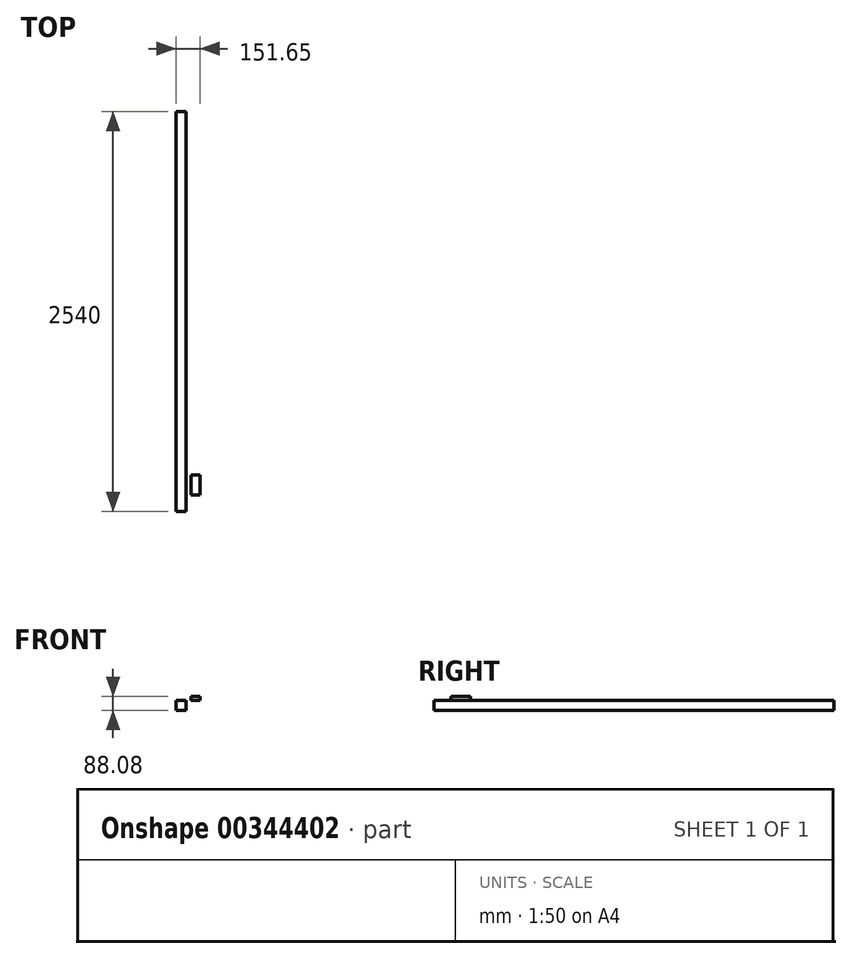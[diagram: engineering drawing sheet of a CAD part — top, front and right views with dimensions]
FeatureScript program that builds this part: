
annotation { "Feature Type Name" : "Feature", "Feature Type Description" : "" }
export const myFeature = defineFeature(function(context is Context, id is Id, definition is map)
    precondition{}
    {
        {
            var Q0;
            Q0=qCreatedBy(makeId("Front.planeOp"),FACE);
            var sketch = newSketch(context, id + "F0", { "sketchPlane" : qUnion([Q0])});
            skLineSegment(sketch, "E0", {"start": v(0, 0) * mm, "end": v(0, 0) * mm});
            skLineSegment(sketch, "E1.bottom", {"start": v(0, 0) * mm, "end": v(62.71, 0) * mm});
            skLineSegment(sketch, "E1.top", {"start": v(0, 62.68) * mm, "end": v(62.71, 62.68) * mm});
            skLineSegment(sketch, "E1.left", {"start": v(0, 0) * mm, "end": v(0, 62.68) * mm});
            skLineSegment(sketch, "E1.right", {"start": v(62.71, 0) * mm, "end": v(62.71, 62.68) * mm});
            skSolve(sketch);
        }
        {
            var Q0;
            Q0 = qSketchRegion(id + "F0", true);
            extrude(context, id + "F1", {"entities" : qUnion([Q0]), "depth" : 2540 * mm});
        }
        {
            var Q0;
            Q0=makeQuery(id+"F1.opExtrude","SWEPT_FACE",FACE,{"disambiguationData":[OSD([sQuery(id+"F0.wireOp",EDGE,"E1.top")])]});
            var sketch = newSketch(context, id + "F2", { "sketchPlane" : qUnion([Q0])});
            skLineSegment(sketch, "E2.bottom", {"start": v(151.65, -2307.67) * mm, "end": v(95.92, -2307.67) * mm});
            skLineSegment(sketch, "E2.top", {"start": v(151.65, -2433.51) * mm, "end": v(95.92, -2433.51) * mm});
            skLineSegment(sketch, "E2.left", {"start": v(151.65, -2307.67) * mm, "end": v(151.65, -2433.51) * mm});
            skLineSegment(sketch, "E2.right", {"start": v(95.92, -2307.67) * mm, "end": v(95.92, -2433.51) * mm});
            skSolve(sketch);
        }
        {
            var Q0;
            Q0 = qSketchRegion(id + "F2", true);
            extrude(context, id + "F3", {"entities" : qUnion([Q0]), "depth" : 25.4 * mm});
        }
    });
